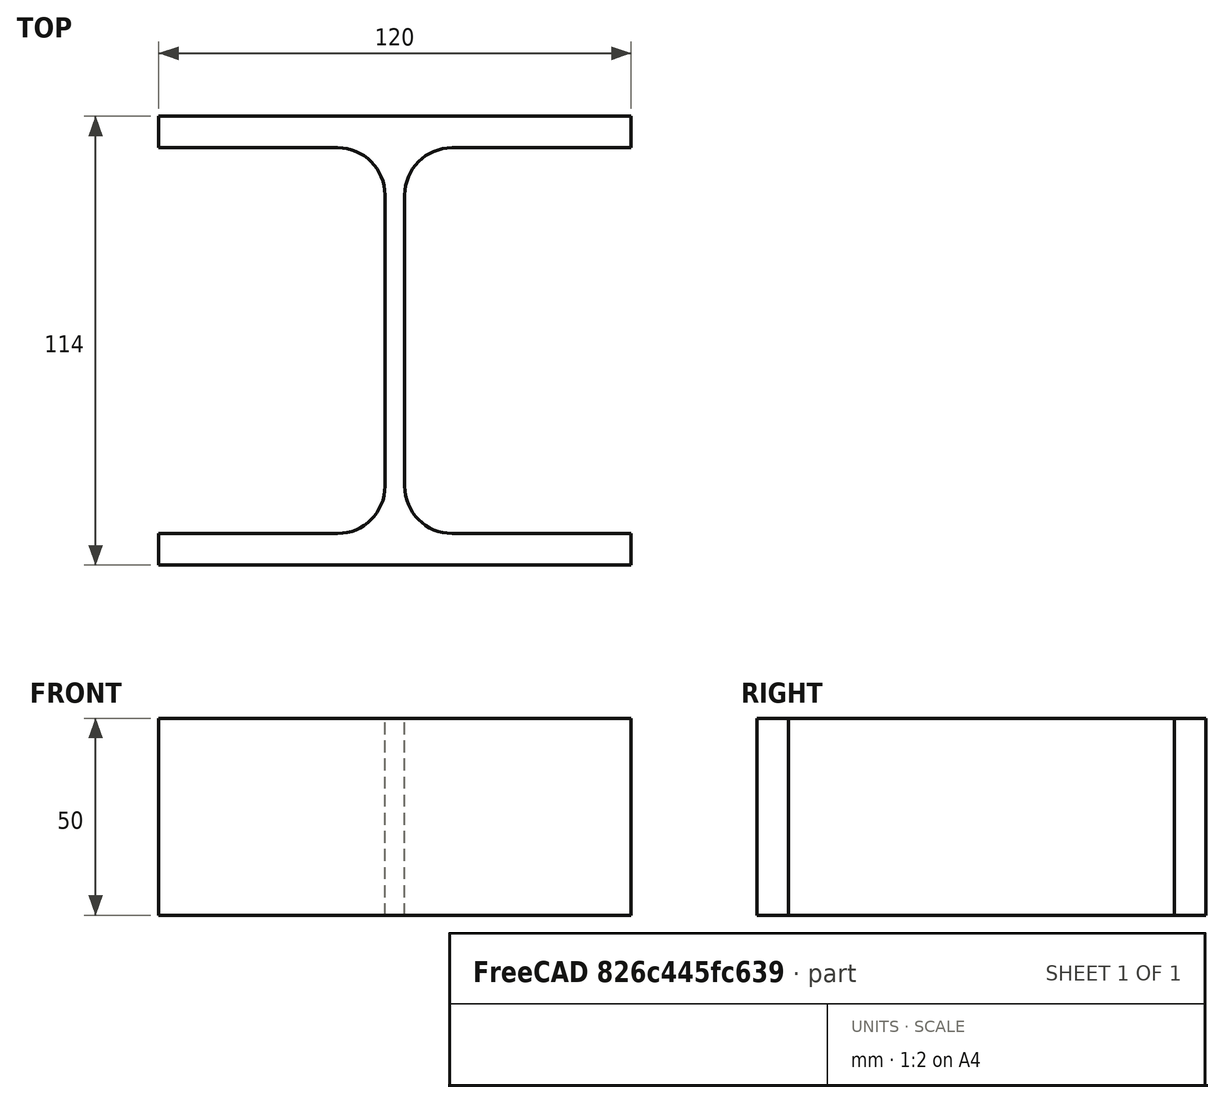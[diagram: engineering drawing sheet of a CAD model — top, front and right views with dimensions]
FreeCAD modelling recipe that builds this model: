
FCSTD DOCUMENT  (FreeCAD 0.15R4671 (Git))
Label: HE-A-Profile 120 DIN1025-3 S235JR
License: All rights reserved
LicenseURL: http://en.wikipedia.org/wiki/All_rights_reserved
objects: Sketcher::SketchObject×1, Part::Extrusion×1
note: 2 computed .brp shape members not serialized (recipe doc carries the construction recipe); baked Part::Feature solids carry a one-line shape summary decoded from their .brp

FEATURE [Sketcher::SketchObject] Sketch
  sketch-geometry (16):
    g0: LineSegment StartX=2.5 StartY=-37 StartZ=0 EndX=2.5 EndY=37 EndZ=0
    g1: LineSegment StartX=14.5 StartY=49 StartZ=0 EndX=60 EndY=49 EndZ=0
    g2: LineSegment StartX=60 StartY=49 StartZ=0 EndX=60 EndY=57 EndZ=0
    g3: LineSegment StartX=60 StartY=57 StartZ=0 EndX=-60 EndY=57 EndZ=0
    g4: LineSegment StartX=-60 StartY=57 StartZ=0 EndX=-60 EndY=49 EndZ=0
    g5: LineSegment StartX=-60 StartY=49 StartZ=0 EndX=-14.5 EndY=49 EndZ=0
    g6: LineSegment StartX=-2.5 StartY=37 StartZ=0 EndX=-2.5 EndY=-37 EndZ=0
    g7: LineSegment StartX=-14.5 StartY=-49 StartZ=0 EndX=-60 EndY=-49 EndZ=0
    g8: LineSegment StartX=-60 StartY=-49 StartZ=0 EndX=-60 EndY=-57 EndZ=0
    g9: LineSegment StartX=-60 StartY=-57 StartZ=0 EndX=60 EndY=-57 EndZ=0
    g10: LineSegment StartX=60 StartY=-57 StartZ=0 EndX=60 EndY=-49 EndZ=0
    g11: LineSegment StartX=60 StartY=-49 StartZ=0 EndX=14.5 EndY=-49 EndZ=0
    g12: ArcOfCircle CenterX=14.5 CenterY=37 CenterZ=0 NormalX=0 NormalY=0 NormalZ=1 Radius=12 StartAngle=1.5708 EndAngle=3.14159
    g13: ArcOfCircle CenterX=14.5 CenterY=-37 CenterZ=0 NormalX=0 NormalY=0 NormalZ=1 Radius=12 StartAngle=3.14159 EndAngle=4.71239
    g14: ArcOfCircle CenterX=-14.5 CenterY=37 CenterZ=0 NormalX=0 NormalY=0 NormalZ=1 Radius=12 StartAngle=0 EndAngle=1.5708
    g15: ArcOfCircle CenterX=-14.5 CenterY=-37 CenterZ=0 NormalX=0 NormalY=0 NormalZ=1 Radius=12 StartAngle=4.71239 EndAngle=6.28319
  constraints (42):
    c: Vertical(g0)
    c: Coincident(g2,g1)
    c: Vertical(g2)
    c: Coincident(g3,g2)
    c: Coincident(g4,g3)
    c: Vertical(g4)
    c: Coincident(g5,g4)
    c: Horizontal(g5)
    c: Vertical(g6)
    c: Horizontal(g7)
    c: Coincident(g8,g7)
    c: Vertical(g8)
    c: Coincident(g9,g8)
    c: Horizontal(g9)
    c: Coincident(g10,g9)
    c: Vertical(g10)
    c: Coincident(g11,g10)
    c: Horizontal(g11)
    c: Tangent(g1,g12) = 1.5708
    c: Tangent(g0,g12) = 1.5708
    c: Tangent(g0,g13) = 1.5708
    c: Tangent(g11,g13) = 1.5708
    c: Tangent(g5,g14) = 1.5708
    c: Tangent(g6,g14) = 1.5708
    c: Tangent(g6,g15) = 1.5708
    c: Tangent(g7,g15) = 1.5708
    c: Equal(g3,g9)
    c: Equal(g2,g4)
    c: Equal(g4,g8)
    c: Equal(g8,g10)
    c: Equal(g12,g14)
    c: Equal(g14,g15)
    c: Equal(g15,g13)
    c: Symmetric(g2,g3,g-2)
    c: Symmetric(g9,g8,g-2)
    c: Symmetric(g0,g6,g-2)
    c: Symmetric(g2,g9,g-1)
    c: DistanceY(g2,g9) = -114
    c: DistanceX(g3) = -120
    c: DistanceX(g0,g6) = -5
    c: DistanceY(g2) = 8
    c: Radius(g12) = 12
FEATURE [Part::Extrusion] Extrude  label="HE-A-Profile 120 DIN1025-3 S235JR"
  Base = -> Sketch
  Dir = (0,0,50)
  Solid = true
